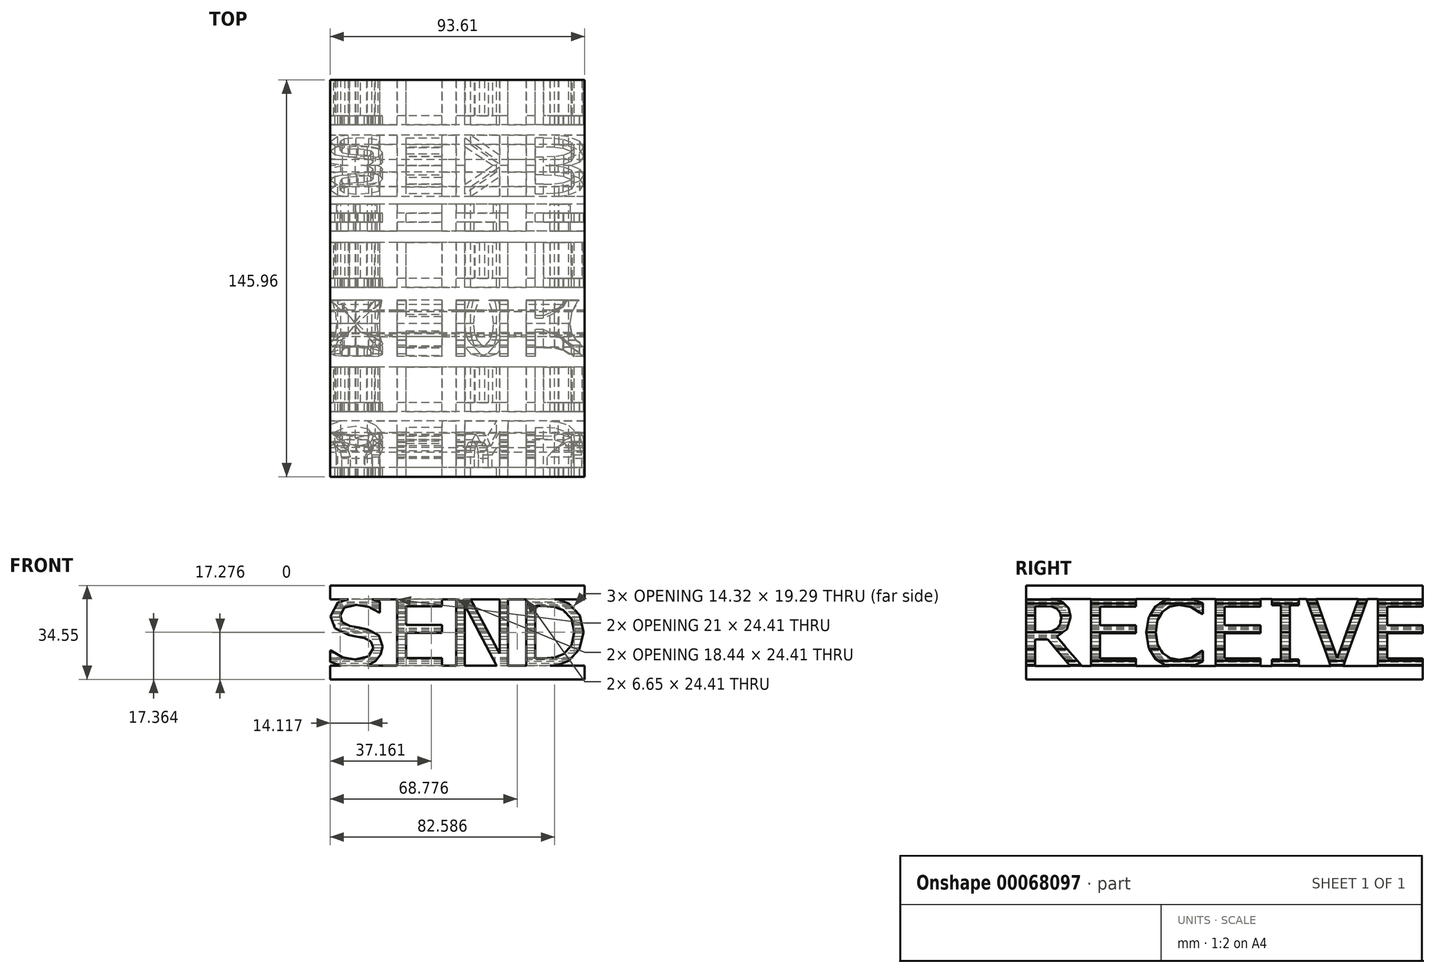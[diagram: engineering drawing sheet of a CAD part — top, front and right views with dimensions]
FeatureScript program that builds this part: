
annotation { "Feature Type Name" : "Feature", "Feature Type Description" : "" }
export const myFeature = defineFeature(function(context is Context, id is Id, definition is map)
    precondition{}
    {
        {
            var Q0;
            Q0=qCreatedBy(makeId("Front.planeOp"),FACE);
            var sketch = newSketch(context, id + "F0", { "sketchPlane" : qUnion([Q0])});
            skLineSegment(sketch, "E0", {"start": v(-25.06, -1.87) * mm, "end": v(-25.75, -4.76) * mm});
            skLineSegment(sketch, "E1", {"start": v(-25.75, -4.76) * mm, "end": v(-27.65, -7.18) * mm});
            skLineSegment(sketch, "E2", {"start": v(-27.65, -7.18) * mm, "end": v(-30.79, -8.85) * mm});
            skLineSegment(sketch, "E3", {"start": v(-35.08, -9.46) * mm, "end": v(-39.95, -8.96) * mm});
            skLineSegment(sketch, "E4", {"start": v(-39.95, -8.96) * mm, "end": v(-44.33, -7.46) * mm});
            skLineSegment(sketch, "E5", {"start": v(-44.33, -7.46) * mm, "end": v(-44.33, -3.3) * mm});
            skLineSegment(sketch, "E6", {"start": v(-769.15, -29.29) * mm, "end": v(-768.92, -29.29) * mm});
            skLineSegment(sketch, "E7", {"start": v(-44.1, -3.3) * mm, "end": v(-39.72, -5.73) * mm});
            skLineSegment(sketch, "E8", {"start": v(-39.72, -5.73) * mm, "end": v(-35.05, -6.59) * mm});
            skLineSegment(sketch, "E9", {"start": v(-35.05, -6.59) * mm, "end": v(-30.25, -5.43) * mm});
            skLineSegment(sketch, "E10", {"start": v(-30.25, -5.43) * mm, "end": v(-28.52, -2.34) * mm});
            skLineSegment(sketch, "E11", {"start": v(-28.52, -2.34) * mm, "end": v(-29.34, 0.11) * mm});
            skLineSegment(sketch, "E12", {"start": v(-29.34, 0.11) * mm, "end": v(-31.8, 1.34) * mm});
            skLineSegment(sketch, "E13", {"start": v(-34.55, 1.9) * mm, "end": v(-37.65, 2.44) * mm});
            skLineSegment(sketch, "E14", {"start": v(-37.65, 2.44) * mm, "end": v(-42.59, 4.85) * mm});
            skLineSegment(sketch, "E15", {"start": v(-42.59, 4.85) * mm, "end": v(-44.18, 9.3) * mm});
            skLineSegment(sketch, "E16", {"start": v(-44.18, 9.3) * mm, "end": v(-41.53, 14.43) * mm});
            skLineSegment(sketch, "E17", {"start": v(-41.53, 14.43) * mm, "end": v(-37.6, 15.61) * mm});
            skLineSegment(sketch, "E18", {"start": v(-34.8, 16.45) * mm, "end": v(-29.96, 15.94) * mm});
            skLineSegment(sketch, "E19", {"start": v(-29.96, 15.94) * mm, "end": v(-26.07, 14.7) * mm});
            skLineSegment(sketch, "E20", {"start": v(-26.07, 14.7) * mm, "end": v(-26.07, 10.77) * mm});
            skLineSegment(sketch, "E21", {"start": v(-675.43, -16.65) * mm, "end": v(-675.67, -16.65) * mm});
            skLineSegment(sketch, "E22", {"start": v(-26.3, 10.77) * mm, "end": v(-30.06, 12.77) * mm});
            skLineSegment(sketch, "E23", {"start": v(-30.06, 12.77) * mm, "end": v(-34.82, 13.58) * mm});
            skLineSegment(sketch, "E24", {"start": v(-34.82, 13.58) * mm, "end": v(-39.11, 12.47) * mm});
            skLineSegment(sketch, "E25", {"start": v(-39.11, 12.47) * mm, "end": v(-40.73, 9.61) * mm});
            skLineSegment(sketch, "E26", {"start": v(-40.73, 9.61) * mm, "end": v(-39.92, 7.16) * mm});
            skLineSegment(sketch, "E27", {"start": v(-39.92, 7.16) * mm, "end": v(-37.08, 5.8) * mm});
            skLineSegment(sketch, "E28", {"start": v(-37.08, 5.8) * mm, "end": v(-34.03, 5.23) * mm});
            skLineSegment(sketch, "E29", {"start": v(-34.03, 5.23) * mm, "end": v(-30.67, 4.54) * mm});
            skLineSegment(sketch, "E30", {"start": v(-30.67, 4.54) * mm, "end": v(-26.47, 2.31) * mm});
            skLineSegment(sketch, "E31", {"start": v(-26.47, 2.31) * mm, "end": v(-25.06, -1.87) * mm});
            skLineSegment(sketch, "E32", {"start": v(-19.72, -9) * mm, "end": v(-19.72, 16) * mm});
            skLineSegment(sketch, "E33", {"start": v(-3.25, 16) * mm, "end": v(-3.25, 13.04) * mm});
            skLineSegment(sketch, "E34", {"start": v(-3.25, 13.04) * mm, "end": v(-16.4, 13.04) * mm});
            skLineSegment(sketch, "E35", {"start": v(-16.4, 13.04) * mm, "end": v(-16.4, 6.19) * mm});
            skLineSegment(sketch, "E36", {"start": v(-16.4, 6.19) * mm, "end": v(-3.25, 6.19) * mm});
            skLineSegment(sketch, "E37", {"start": v(-3.25, 6.19) * mm, "end": v(-3.25, 3.23) * mm});
            skLineSegment(sketch, "E38", {"start": v(-3.25, 3.23) * mm, "end": v(-16.4, 3.23) * mm});
            skLineSegment(sketch, "E39", {"start": v(-16.4, 3.23) * mm, "end": v(-16.4, -6.05) * mm});
            skLineSegment(sketch, "E40", {"start": v(-16.4, -6.05) * mm, "end": v(-3.25, -6.05) * mm});
            skLineSegment(sketch, "E41", {"start": v(-3.25, -6.05) * mm, "end": v(-3.25, -9) * mm});
            skLineSegment(sketch, "E42", {"start": v(17, -9) * mm, "end": v(5.14, 13.36) * mm});
            skLineSegment(sketch, "E43", {"start": v(5.14, 13.36) * mm, "end": v(5.14, -9) * mm});
            skLineSegment(sketch, "E44", {"start": v(2.04, -9) * mm, "end": v(2.04, 16) * mm});
            skLineSegment(sketch, "E45", {"start": v(7.2, 16) * mm, "end": v(18, -4.42) * mm});
            skLineSegment(sketch, "E46", {"start": v(18, -4.42) * mm, "end": v(18, 16) * mm});
            skLineSegment(sketch, "E47", {"start": v(21.11, 16) * mm, "end": v(21.11, -9) * mm});
            skLineSegment(sketch, "E48", {"start": v(48.88, 3.47) * mm, "end": v(47.39, -2.7) * mm});
            skLineSegment(sketch, "E49", {"start": v(47.39, -2.7) * mm, "end": v(43.44, -7) * mm});
            skLineSegment(sketch, "E50", {"start": v(43.44, -7) * mm, "end": v(39.61, -8.54) * mm});
            skLineSegment(sketch, "E51", {"start": v(39.61, -8.54) * mm, "end": v(34.07, -9) * mm});
            skLineSegment(sketch, "E52", {"start": v(27.76, -9) * mm, "end": v(27.76, 16) * mm});
            skLineSegment(sketch, "E53", {"start": v(34, 16) * mm, "end": v(39.82, 15.46) * mm});
            skLineSegment(sketch, "E54", {"start": v(39.82, 15.46) * mm, "end": v(43.48, 14.01) * mm});
            skLineSegment(sketch, "E55", {"start": v(43.48, 14.01) * mm, "end": v(47.45, 9.77) * mm});
            skLineSegment(sketch, "E56", {"start": v(47.45, 9.77) * mm, "end": v(48.88, 3.47) * mm});
            skLineSegment(sketch, "E57", {"start": v(45.4, 3.52) * mm, "end": v(44.38, 8.47) * mm});
            skLineSegment(sketch, "E58", {"start": v(44.38, 8.47) * mm, "end": v(41.33, 11.65) * mm});
            skLineSegment(sketch, "E59", {"start": v(41.33, 11.65) * mm, "end": v(38.19, 12.8) * mm});
            skLineSegment(sketch, "E60", {"start": v(38.19, 12.8) * mm, "end": v(34.2, 13.14) * mm});
            skLineSegment(sketch, "E61", {"start": v(31.08, 13.14) * mm, "end": v(31.08, -6.15) * mm});
            skLineSegment(sketch, "E62", {"start": v(34.2, -6.15) * mm, "end": v(38.39, -5.8) * mm});
            skLineSegment(sketch, "E63", {"start": v(38.39, -5.8) * mm, "end": v(41.68, -4.49) * mm});
            skLineSegment(sketch, "E64", {"start": v(41.68, -4.49) * mm, "end": v(44.47, -1.35) * mm});
            skLineSegment(sketch, "E65", {"start": v(44.47, -1.35) * mm, "end": v(45.4, 3.52) * mm});
            skLineSegment(sketch, "E66", {"start": v(-581.37, -15.69) * mm, "end": v(-581.63, -15.69) * mm});
            skLineSegment(sketch, "E67", {"start": v(-581.6, -29.29) * mm, "end": v(-581.37, -29.29) * mm});
            skLineSegment(sketch, "E68", {"start": v(-34.55, 1.9) * mm, "end": v(-31.8, 1.34) * mm});
            skLineSegment(sketch, "E69", {"start": v(-44.33, -3.3) * mm, "end": v(-44.1, -3.3) * mm});
            skLineSegment(sketch, "E70", {"start": v(-26.3, 10.77) * mm, "end": v(-26.07, 10.77) * mm});
            skLineSegment(sketch, "E71.bottom", {"start": v(-44.34, -13.87) * mm, "end": v(49.27, -13.87) * mm});
            skLineSegment(sketch, "E71.top", {"start": v(-44.34, -8.8) * mm, "end": v(-40.41, -8.8) * mm});
            skLineSegment(sketch, "E71.left", {"start": v(-44.34, -13.87) * mm, "end": v(-44.34, -8.8) * mm});
            skLineSegment(sketch, "E71.right", {"start": v(49.27, -13.87) * mm, "end": v(49.27, -8.8) * mm});
            skLineSegment(sketch, "E72", {"start": v(31.08, 13.14) * mm, "end": v(34.2, 13.14) * mm});
            skLineSegment(sketch, "E73", {"start": v(34.2, -6.15) * mm, "end": v(31.08, -6.15) * mm});
            skLineSegment(sketch, "E74.bottom", {"start": v(-44.34, 15.61) * mm, "end": v(-37.6, 15.61) * mm});
            skLineSegment(sketch, "E74.top", {"start": v(-44.34, 20.68) * mm, "end": v(49.27, 20.68) * mm});
            skLineSegment(sketch, "E74.left", {"start": v(-44.34, 15.61) * mm, "end": v(-44.34, 20.68) * mm});
            skLineSegment(sketch, "E74.right", {"start": v(49.27, 15.61) * mm, "end": v(49.27, 20.68) * mm});
            skLineSegment(sketch, "E75.trimOffspring", {"start": v(-28.92, 15.61) * mm, "end": v(-19.72, 15.61) * mm});
            skLineSegment(sketch, "E76.trimOffspring", {"start": v(-30.68, -8.8) * mm, "end": v(-19.72, -8.8) * mm});
            skLineSegment(sketch, "E77.trimOffspring", {"start": v(-3.25, -8.8) * mm, "end": v(2.04, -8.8) * mm});
            skLineSegment(sketch, "E78.trimOffspring", {"start": v(5.14, -8.8) * mm, "end": v(16.89, -8.8) * mm});
            skLineSegment(sketch, "E79.trimOffspring", {"start": v(-3.25, 15.61) * mm, "end": v(2.04, 15.61) * mm});
            skLineSegment(sketch, "E80.trimOffspring", {"start": v(7.4, 15.61) * mm, "end": v(18, 15.61) * mm});
            skLineSegment(sketch, "E81.trimOffspring", {"start": v(21.11, -8.8) * mm, "end": v(27.76, -8.8) * mm});
            skLineSegment(sketch, "E82.trimOffspring", {"start": v(21.11, 15.61) * mm, "end": v(27.76, 15.61) * mm});
            skLineSegment(sketch, "E83.trimOffspring", {"start": v(38.14, 15.61) * mm, "end": v(49.27, 15.61) * mm});
            skLineSegment(sketch, "E84.trimOffspring", {"start": v(36.5, -8.8) * mm, "end": v(49.27, -8.8) * mm});
            skSolve(sketch);
        }
        {
            var Q0;
            Q0=makeQuery(id+"F0.imprint","IMPRINT",FACE,{"disambiguationData":[TD([[makeQuery(id+"F0.imprint","IMPRINT",EDGE,{"derivedFrom":sQuery(id+"F0.wireOp",EDGE,"E0")}),-1.0]])]});
            extrude(context, id + "F1", {"entities" : qUnion([Q0]), "endBound" : BoundingType.SYMMETRIC, "depth" : 205 * mm});
        }
        {
            var Q0;
            Q0=qCreatedBy(makeId("Right.planeOp"),FACE);
            var sketch = newSketch(context, id + "F2", { "sketchPlane" : qUnion([Q0])});
            skLineSegment(sketch, "E85", {"start": v(-134.38, -6.8) * mm, "end": v(-134.14, -6.8) * mm});
            skLineSegment(sketch, "E86", {"start": v(-116.1, 7.28) * mm, "end": v(-116.34, 7.28) * mm});
            skLineSegment(sketch, "E87", {"start": v(-43.67, -9.1) * mm, "end": v(-52.03, 0.84) * mm});
            skLineSegment(sketch, "E88", {"start": v(-52.03, 0.84) * mm, "end": v(-56.71, 0.84) * mm});
            skLineSegment(sketch, "E89", {"start": v(-56.71, 0.84) * mm, "end": v(-56.71, -9.1) * mm});
            skLineSegment(sketch, "E90", {"start": v(-60.04, -8.72) * mm, "end": v(-60.04, 16.28) * mm});
            skLineSegment(sketch, "E91", {"start": v(-53.04, 15.9) * mm, "end": v(-49.26, 15.6) * mm});
            skLineSegment(sketch, "E92", {"start": v(-49.26, 15.6) * mm, "end": v(-46.54, 14.55) * mm});
            skLineSegment(sketch, "E93", {"start": v(-46.54, 14.55) * mm, "end": v(-44.42, 12.39) * mm});
            skLineSegment(sketch, "E94", {"start": v(-44.42, 12.39) * mm, "end": v(-43.65, 9.1) * mm});
            skLineSegment(sketch, "E95", {"start": v(-43.65, 9.1) * mm, "end": v(-45, 4.56) * mm});
            skLineSegment(sketch, "E96", {"start": v(-45, 4.56) * mm, "end": v(-48.75, 1.83) * mm});
            skLineSegment(sketch, "E97", {"start": v(-48.75, 1.83) * mm, "end": v(-39.35, -9.1) * mm});
            skLineSegment(sketch, "E98", {"start": v(-47.13, 8.86) * mm, "end": v(-47.51, 10.76) * mm});
            skLineSegment(sketch, "E99", {"start": v(-47.51, 10.76) * mm, "end": v(-48.75, 12.17) * mm});
            skLineSegment(sketch, "E100", {"start": v(-48.75, 12.17) * mm, "end": v(-50.47, 12.84) * mm});
            skLineSegment(sketch, "E101", {"start": v(-50.47, 12.84) * mm, "end": v(-52.8, 13.04) * mm});
            skLineSegment(sketch, "E102", {"start": v(-52.8, 13.04) * mm, "end": v(-56.71, 13.04) * mm});
            skLineSegment(sketch, "E103", {"start": v(-56.71, 13.04) * mm, "end": v(-56.71, 3.6) * mm});
            skLineSegment(sketch, "E104", {"start": v(-56.71, 3.6) * mm, "end": v(-53.35, 3.6) * mm});
            skLineSegment(sketch, "E105", {"start": v(-53.35, 3.6) * mm, "end": v(-50.6, 3.87) * mm});
            skLineSegment(sketch, "E106", {"start": v(-50.6, 3.87) * mm, "end": v(-48.6, 4.92) * mm});
            skLineSegment(sketch, "E107", {"start": v(-48.6, 4.92) * mm, "end": v(-47.5, 6.53) * mm});
            skLineSegment(sketch, "E108", {"start": v(-47.5, 6.53) * mm, "end": v(-47.13, 8.86) * mm});
            skLineSegment(sketch, "E109", {"start": v(-36.13, -9.1) * mm, "end": v(-36.13, 15.9) * mm});
            skLineSegment(sketch, "E110", {"start": v(-19.66, 15.9) * mm, "end": v(-19.66, 12.94) * mm});
            skLineSegment(sketch, "E111", {"start": v(-19.66, 12.94) * mm, "end": v(-32.8, 12.94) * mm});
            skLineSegment(sketch, "E112", {"start": v(-32.8, 12.94) * mm, "end": v(-32.8, 6.1) * mm});
            skLineSegment(sketch, "E113", {"start": v(-32.8, 6.1) * mm, "end": v(-19.66, 6.1) * mm});
            skLineSegment(sketch, "E114", {"start": v(-19.66, 6.1) * mm, "end": v(-19.66, 3.14) * mm});
            skLineSegment(sketch, "E115", {"start": v(-19.66, 3.14) * mm, "end": v(-32.8, 3.14) * mm});
            skLineSegment(sketch, "E116", {"start": v(-32.8, 3.14) * mm, "end": v(-32.8, -6.15) * mm});
            skLineSegment(sketch, "E117", {"start": v(-32.8, -6.15) * mm, "end": v(-19.66, -6.15) * mm});
            skLineSegment(sketch, "E118", {"start": v(-19.66, -6.15) * mm, "end": v(-19.66, -9.1) * mm});
            skLineSegment(sketch, "E119", {"start": v(4.94, -7.3) * mm, "end": v(3.26, -8.05) * mm});
            skLineSegment(sketch, "E120", {"start": v(3.26, -8.05) * mm, "end": v(1.31, -8.78) * mm});
            skLineSegment(sketch, "E121", {"start": v(1.31, -8.78) * mm, "end": v(-0.92, -9.32) * mm});
            skLineSegment(sketch, "E122", {"start": v(-3.56, -9.56) * mm, "end": v(-8.5, -8.8) * mm});
            skLineSegment(sketch, "E123", {"start": v(-8.5, -8.8) * mm, "end": v(-12.37, -6.4) * mm});
            skLineSegment(sketch, "E124", {"start": v(-12.37, -6.4) * mm, "end": v(-14.89, -2.35) * mm});
            skLineSegment(sketch, "E125", {"start": v(-14.89, -2.35) * mm, "end": v(-15.8, 3.37) * mm});
            skLineSegment(sketch, "E126", {"start": v(-15.8, 3.37) * mm, "end": v(-14.92, 8.9) * mm});
            skLineSegment(sketch, "E127", {"start": v(-14.92, 8.9) * mm, "end": v(-12.4, 13) * mm});
            skLineSegment(sketch, "E128", {"start": v(-12.4, 13) * mm, "end": v(-8.56, 15.5) * mm});
            skLineSegment(sketch, "E129", {"start": v(-8.56, 15.5) * mm, "end": v(-3.54, 16.35) * mm});
            skLineSegment(sketch, "E130", {"start": v(0.47, 15.86) * mm, "end": v(4.94, 14.15) * mm});
            skLineSegment(sketch, "E131", {"start": v(4.94, 14.15) * mm, "end": v(4.94, 10.2) * mm});
            skLineSegment(sketch, "E132", {"start": v(53.4, 6.8) * mm, "end": v(53.15, 6.8) * mm});
            skLineSegment(sketch, "E133", {"start": v(4.69, 10.2) * mm, "end": v(0.6, 12.72) * mm});
            skLineSegment(sketch, "E134", {"start": v(0.6, 12.72) * mm, "end": v(-3.76, 13.51) * mm});
            skLineSegment(sketch, "E135", {"start": v(-3.76, 13.51) * mm, "end": v(-7.18, 12.9) * mm});
            skLineSegment(sketch, "E136", {"start": v(-7.18, 12.9) * mm, "end": v(-9.89, 11) * mm});
            skLineSegment(sketch, "E137", {"start": v(-9.89, 11) * mm, "end": v(-11.7, 7.8) * mm});
            skLineSegment(sketch, "E138", {"start": v(-11.7, 7.8) * mm, "end": v(-12.34, 3.37) * mm});
            skLineSegment(sketch, "E139", {"start": v(-12.34, 3.37) * mm, "end": v(-11.63, -1.16) * mm});
            skLineSegment(sketch, "E140", {"start": v(-11.63, -1.16) * mm, "end": v(-9.78, -4.25) * mm});
            skLineSegment(sketch, "E141", {"start": v(-9.78, -4.25) * mm, "end": v(-7.05, -6.1) * mm});
            skLineSegment(sketch, "E142", {"start": v(-7.05, -6.1) * mm, "end": v(-3.72, -6.69) * mm});
            skLineSegment(sketch, "E143", {"start": v(-3.72, -6.69) * mm, "end": v(0.78, -5.86) * mm});
            skLineSegment(sketch, "E144", {"start": v(0.78, -5.86) * mm, "end": v(4.7, -3.4) * mm});
            skLineSegment(sketch, "E145", {"start": v(53.16, -6.8) * mm, "end": v(53.4, -6.8) * mm});
            skLineSegment(sketch, "E146", {"start": v(4.94, -3.4) * mm, "end": v(4.94, -7.3) * mm});
            skLineSegment(sketch, "E147", {"start": v(9.67, -9.1) * mm, "end": v(9.67, 15.9) * mm});
            skLineSegment(sketch, "E148", {"start": v(26.15, 15.9) * mm, "end": v(26.15, 12.94) * mm});
            skLineSegment(sketch, "E149", {"start": v(26.15, 12.94) * mm, "end": v(13, 12.94) * mm});
            skLineSegment(sketch, "E150", {"start": v(13, 12.94) * mm, "end": v(13, 6.1) * mm});
            skLineSegment(sketch, "E151", {"start": v(13, 6.1) * mm, "end": v(26.15, 6.1) * mm});
            skLineSegment(sketch, "E152", {"start": v(26.15, 6.1) * mm, "end": v(26.15, 3.14) * mm});
            skLineSegment(sketch, "E153", {"start": v(26.15, 3.14) * mm, "end": v(13, 3.14) * mm});
            skLineSegment(sketch, "E154", {"start": v(13, 3.14) * mm, "end": v(13, -6.15) * mm});
            skLineSegment(sketch, "E155", {"start": v(13, -6.15) * mm, "end": v(26.15, -6.15) * mm});
            skLineSegment(sketch, "E156", {"start": v(26.15, -6.15) * mm, "end": v(26.15, -9.1) * mm});
            skLineSegment(sketch, "E157", {"start": v(30.38, -9.1) * mm, "end": v(30.38, -6.55) * mm});
            skLineSegment(sketch, "E158", {"start": v(30.38, -6.55) * mm, "end": v(33.65, -6.55) * mm});
            skLineSegment(sketch, "E159", {"start": v(33.65, -6.55) * mm, "end": v(33.65, 13.34) * mm});
            skLineSegment(sketch, "E160", {"start": v(33.65, 13.34) * mm, "end": v(30.38, 13.34) * mm});
            skLineSegment(sketch, "E161", {"start": v(30.38, 13.34) * mm, "end": v(30.38, 15.9) * mm});
            skLineSegment(sketch, "E162", {"start": v(40.25, 15.9) * mm, "end": v(40.25, 13.34) * mm});
            skLineSegment(sketch, "E163", {"start": v(40.25, 13.34) * mm, "end": v(36.97, 13.34) * mm});
            skLineSegment(sketch, "E164", {"start": v(36.97, 13.34) * mm, "end": v(36.97, -6.55) * mm});
            skLineSegment(sketch, "E165", {"start": v(36.97, -6.55) * mm, "end": v(40.25, -6.55) * mm});
            skLineSegment(sketch, "E166", {"start": v(40.25, -6.55) * mm, "end": v(40.25, -9.1) * mm});
            skLineSegment(sketch, "E167", {"start": v(65.65, 15.9) * mm, "end": v(56.55, -9.1) * mm});
            skLineSegment(sketch, "E168", {"start": v(52.12, -9.1) * mm, "end": v(43.02, 15.9) * mm});
            skLineSegment(sketch, "E169", {"start": v(46.58, 15.9) * mm, "end": v(54.42, -6.1) * mm});
            skLineSegment(sketch, "E170", {"start": v(54.42, -6.1) * mm, "end": v(62.26, 15.9) * mm});
            skLineSegment(sketch, "E171", {"start": v(69.45, -9.1) * mm, "end": v(69.45, 15.9) * mm});
            skLineSegment(sketch, "E172", {"start": v(85.92, 15.9) * mm, "end": v(85.92, 12.94) * mm});
            skLineSegment(sketch, "E173", {"start": v(85.92, 12.94) * mm, "end": v(72.77, 12.94) * mm});
            skLineSegment(sketch, "E174", {"start": v(72.77, 12.94) * mm, "end": v(72.77, 6.1) * mm});
            skLineSegment(sketch, "E175", {"start": v(72.77, 6.1) * mm, "end": v(85.92, 6.1) * mm});
            skLineSegment(sketch, "E176", {"start": v(85.92, 6.1) * mm, "end": v(85.92, 3.14) * mm});
            skLineSegment(sketch, "E177", {"start": v(85.92, 3.14) * mm, "end": v(72.77, 3.14) * mm});
            skLineSegment(sketch, "E178", {"start": v(72.77, 3.14) * mm, "end": v(72.77, -6.15) * mm});
            skLineSegment(sketch, "E179", {"start": v(72.77, -6.15) * mm, "end": v(85.92, -6.15) * mm});
            skLineSegment(sketch, "E180", {"start": v(85.92, -6.15) * mm, "end": v(85.92, -9.1) * mm});
            skLineSegment(sketch, "E181.bottom", {"start": v(-51, 15.73) * mm, "end": v(-36.13, 15.73) * mm});
            skLineSegment(sketch, "E181.top", {"start": v(-60.04, 20.73) * mm, "end": v(85.92, 20.73) * mm});
            skLineSegment(sketch, "E181.left", {"start": v(-60.04, 15.73) * mm, "end": v(-60.04, 20.73) * mm});
            skLineSegment(sketch, "E181.right", {"start": v(85.92, 15.73) * mm, "end": v(85.92, 20.73) * mm});
            skLineSegment(sketch, "E182.bottom", {"start": v(-56.71, -8.96) * mm, "end": v(-43.78, -8.96) * mm});
            skLineSegment(sketch, "E182.top", {"start": v(-60.04, -13.96) * mm, "end": v(85.92, -13.96) * mm});
            skLineSegment(sketch, "E182.left", {"start": v(-60.04, -8.96) * mm, "end": v(-60.04, -13.96) * mm});
            skLineSegment(sketch, "E182.right", {"start": v(85.92, -8.96) * mm, "end": v(85.92, -13.96) * mm});
            skLineSegment(sketch, "E183", {"start": v(-60.04, -9.1) * mm, "end": v(-60.04, -8.72) * mm});
            skLineSegment(sketch, "E184.trimOffspring", {"start": v(-39.47, -8.96) * mm, "end": v(-36.13, -8.96) * mm});
            skLineSegment(sketch, "E185.trimOffspring", {"start": v(-19.66, -8.96) * mm, "end": v(-7.45, -8.96) * mm});
            skPoint(sketch, "E186.start.orphan", {"position": v(-60.04, 15.9) * mm});
            skLineSegment(sketch, "E187.trimOffspring", {"start": v(-19.66, 15.73) * mm, "end": v(-7.15, 15.73) * mm});
            skLineSegment(sketch, "E188.trimOffspring", {"start": v(0.8, 15.73) * mm, "end": v(9.67, 15.73) * mm});
            skLineSegment(sketch, "E189.trimOffspring", {"start": v(0.57, -8.96) * mm, "end": v(9.67, -8.96) * mm});
            skLineSegment(sketch, "E190.trimOffspring", {"start": v(26.15, 15.73) * mm, "end": v(30.38, 15.73) * mm});
            skLineSegment(sketch, "E191.trimOffspring", {"start": v(40.25, 15.73) * mm, "end": v(43.08, 15.73) * mm});
            skLineSegment(sketch, "E192.trimOffspring", {"start": v(46.64, 15.73) * mm, "end": v(62.2, 15.73) * mm});
            skLineSegment(sketch, "E193.trimOffspring", {"start": v(26.15, -8.96) * mm, "end": v(30.38, -8.96) * mm});
            skLineSegment(sketch, "E194.trimOffspring", {"start": v(40.25, -8.96) * mm, "end": v(52.07, -8.96) * mm});
            skLineSegment(sketch, "E195.trimOffspring", {"start": v(56.6, -8.96) * mm, "end": v(69.45, -8.96) * mm});
            skLineSegment(sketch, "E196.trimOffspring", {"start": v(65.6, 15.73) * mm, "end": v(69.45, 15.73) * mm});
            skPoint(sketch, "E197.end.orphan", {"position": v(85.92, 16.28) * mm});
            skPoint(sketch, "E198.start.orphan", {"position": v(85.92, -9.1) * mm});
            skLineSegment(sketch, "E199", {"start": v(4.7, -3.4) * mm, "end": v(4.94, -3.4) * mm});
            skLineSegment(sketch, "E200", {"start": v(4.69, 10.2) * mm, "end": v(4.94, 10.2) * mm});
            skSolve(sketch);
        }
        {
            var Q0;
            {var subQ38=sQuery(id+"F2.wireOp",EDGE,"E88");Q0=makeQuery(id+"F2.imprint","IMPRINT",FACE,{"disambiguationData":[TD([[makeQuery(id+"F2.imprint","IMPRINT",EDGE,{"derivedFrom":subQ38}),-1.0]])]});}
            extrude(context, id + "F3", {"entities" : qUnion([Q0]), "endBound" : BoundingType.SYMMETRIC, "depth" : 222 * mm});
        }
        {
            var Q0;
            Q0=makeQuery(id+"F1.opExtrude","SWEPT_BODY",BODY,{"disambiguationData":[OSD([sQuery(id+"F0.wireOp",EDGE,"E0"),sQuery(id+"F0.wireOp",EDGE,"E1"),sQuery(id+"F0.wireOp",EDGE,"E2"),sQuery(id+"F0.wireOp",EDGE,"E4"),sQuery(id+"F0.wireOp",EDGE,"E5"),sQuery(id+"F0.wireOp",EDGE,"E7"),sQuery(id+"F0.wireOp",EDGE,"E8"),sQuery(id+"F0.wireOp",EDGE,"E9"),sQuery(id+"F0.wireOp",EDGE,"E10"),sQuery(id+"F0.wireOp",EDGE,"E11"),sQuery(id+"F0.wireOp",EDGE,"E12"),sQuery(id+"F0.wireOp",EDGE,"E13"),sQuery(id+"F0.wireOp",EDGE,"E14"),sQuery(id+"F0.wireOp",EDGE,"E15"),sQuery(id+"F0.wireOp",EDGE,"E16"),sQuery(id+"F0.wireOp",EDGE,"E17"),sQuery(id+"F0.wireOp",EDGE,"E19"),sQuery(id+"F0.wireOp",EDGE,"E20"),sQuery(id+"F0.wireOp",EDGE,"E22"),sQuery(id+"F0.wireOp",EDGE,"E23"),sQuery(id+"F0.wireOp",EDGE,"E24"),sQuery(id+"F0.wireOp",EDGE,"E25"),sQuery(id+"F0.wireOp",EDGE,"E26"),sQuery(id+"F0.wireOp",EDGE,"E27"),sQuery(id+"F0.wireOp",EDGE,"E28"),sQuery(id+"F0.wireOp",EDGE,"E29"),sQuery(id+"F0.wireOp",EDGE,"E30"),sQuery(id+"F0.wireOp",EDGE,"E31"),sQuery(id+"F0.wireOp",EDGE,"E32"),sQuery(id+"F0.wireOp",EDGE,"E33"),sQuery(id+"F0.wireOp",EDGE,"E34"),sQuery(id+"F0.wireOp",EDGE,"E35"),sQuery(id+"F0.wireOp",EDGE,"E36"),sQuery(id+"F0.wireOp",EDGE,"E37"),sQuery(id+"F0.wireOp",EDGE,"E38"),sQuery(id+"F0.wireOp",EDGE,"E39"),sQuery(id+"F0.wireOp",EDGE,"E40"),sQuery(id+"F0.wireOp",EDGE,"E41"),sQuery(id+"F0.wireOp",EDGE,"E42"),sQuery(id+"F0.wireOp",EDGE,"E43"),sQuery(id+"F0.wireOp",EDGE,"E44"),sQuery(id+"F0.wireOp",EDGE,"E45"),sQuery(id+"F0.wireOp",EDGE,"E46"),sQuery(id+"F0.wireOp",EDGE,"E47"),sQuery(id+"F0.wireOp",EDGE,"E48"),sQuery(id+"F0.wireOp",EDGE,"E49"),sQuery(id+"F0.wireOp",EDGE,"E50"),sQuery(id+"F0.wireOp",EDGE,"E51"),sQuery(id+"F0.wireOp",EDGE,"E52"),sQuery(id+"F0.wireOp",EDGE,"E53"),sQuery(id+"F0.wireOp",EDGE,"E54"),sQuery(id+"F0.wireOp",EDGE,"E55"),sQuery(id+"F0.wireOp",EDGE,"E56"),sQuery(id+"F0.wireOp",EDGE,"E57"),sQuery(id+"F0.wireOp",EDGE,"E58"),sQuery(id+"F0.wireOp",EDGE,"E59"),sQuery(id+"F0.wireOp",EDGE,"E60"),sQuery(id+"F0.wireOp",EDGE,"E61"),sQuery(id+"F0.wireOp",EDGE,"E62"),sQuery(id+"F0.wireOp",EDGE,"E63"),sQuery(id+"F0.wireOp",EDGE,"E64"),sQuery(id+"F0.wireOp",EDGE,"E65"),sQuery(id+"F0.wireOp",EDGE,"E68"),sQuery(id+"F0.wireOp",EDGE,"E69"),sQuery(id+"F0.wireOp",EDGE,"E70"),sQuery(id+"F0.wireOp",EDGE,"E71.bottom"),sQuery(id+"F0.wireOp",EDGE,"E71.top"),sQuery(id+"F0.wireOp",EDGE,"E71.left"),sQuery(id+"F0.wireOp",EDGE,"E71.right"),sQuery(id+"F0.wireOp",EDGE,"E72"),sQuery(id+"F0.wireOp",EDGE,"E73"),sQuery(id+"F0.wireOp",EDGE,"E74.bottom"),sQuery(id+"F0.wireOp",EDGE,"E74.top"),sQuery(id+"F0.wireOp",EDGE,"E74.left"),sQuery(id+"F0.wireOp",EDGE,"E74.right"),sQuery(id+"F0.wireOp",EDGE,"E75.trimOffspring"),sQuery(id+"F0.wireOp",EDGE,"E76.trimOffspring"),sQuery(id+"F0.wireOp",EDGE,"E77.trimOffspring"),sQuery(id+"F0.wireOp",EDGE,"E78.trimOffspring"),sQuery(id+"F0.wireOp",EDGE,"E79.trimOffspring"),sQuery(id+"F0.wireOp",EDGE,"E80.trimOffspring"),sQuery(id+"F0.wireOp",EDGE,"E81.trimOffspring"),sQuery(id+"F0.wireOp",EDGE,"E82.trimOffspring"),sQuery(id+"F0.wireOp",EDGE,"E83.trimOffspring"),sQuery(id+"F0.wireOp",EDGE,"E84.trimOffspring")])]});
            var Q1;
            Q1=makeQuery(id+"F3.opExtrude","SWEPT_BODY",BODY,{"disambiguationData":[OSD([sQuery(id+"F2.wireOp",EDGE,"E87"),sQuery(id+"F2.wireOp",EDGE,"E88"),sQuery(id+"F2.wireOp",EDGE,"E89"),sQuery(id+"F2.wireOp",EDGE,"E90"),sQuery(id+"F2.wireOp",EDGE,"E91"),sQuery(id+"F2.wireOp",EDGE,"E92"),sQuery(id+"F2.wireOp",EDGE,"E93"),sQuery(id+"F2.wireOp",EDGE,"E94"),sQuery(id+"F2.wireOp",EDGE,"E95"),sQuery(id+"F2.wireOp",EDGE,"E96"),sQuery(id+"F2.wireOp",EDGE,"E97"),sQuery(id+"F2.wireOp",EDGE,"E98"),sQuery(id+"F2.wireOp",EDGE,"E99"),sQuery(id+"F2.wireOp",EDGE,"E100"),sQuery(id+"F2.wireOp",EDGE,"E101"),sQuery(id+"F2.wireOp",EDGE,"E102"),sQuery(id+"F2.wireOp",EDGE,"E103"),sQuery(id+"F2.wireOp",EDGE,"E104"),sQuery(id+"F2.wireOp",EDGE,"E105"),sQuery(id+"F2.wireOp",EDGE,"E106"),sQuery(id+"F2.wireOp",EDGE,"E107"),sQuery(id+"F2.wireOp",EDGE,"E108"),sQuery(id+"F2.wireOp",EDGE,"E109"),sQuery(id+"F2.wireOp",EDGE,"E110"),sQuery(id+"F2.wireOp",EDGE,"E111"),sQuery(id+"F2.wireOp",EDGE,"E112"),sQuery(id+"F2.wireOp",EDGE,"E113"),sQuery(id+"F2.wireOp",EDGE,"E114"),sQuery(id+"F2.wireOp",EDGE,"E115"),sQuery(id+"F2.wireOp",EDGE,"E116"),sQuery(id+"F2.wireOp",EDGE,"E117"),sQuery(id+"F2.wireOp",EDGE,"E118"),sQuery(id+"F2.wireOp",EDGE,"E119"),sQuery(id+"F2.wireOp",EDGE,"E120"),sQuery(id+"F2.wireOp",EDGE,"E121"),sQuery(id+"F2.wireOp",EDGE,"E122"),sQuery(id+"F2.wireOp",EDGE,"E123"),sQuery(id+"F2.wireOp",EDGE,"E124"),sQuery(id+"F2.wireOp",EDGE,"E125"),sQuery(id+"F2.wireOp",EDGE,"E126"),sQuery(id+"F2.wireOp",EDGE,"E127"),sQuery(id+"F2.wireOp",EDGE,"E128"),sQuery(id+"F2.wireOp",EDGE,"E129"),sQuery(id+"F2.wireOp",EDGE,"E130"),sQuery(id+"F2.wireOp",EDGE,"E131"),sQuery(id+"F2.wireOp",EDGE,"E133"),sQuery(id+"F2.wireOp",EDGE,"E134"),sQuery(id+"F2.wireOp",EDGE,"E135"),sQuery(id+"F2.wireOp",EDGE,"E136"),sQuery(id+"F2.wireOp",EDGE,"E137"),sQuery(id+"F2.wireOp",EDGE,"E138"),sQuery(id+"F2.wireOp",EDGE,"E139"),sQuery(id+"F2.wireOp",EDGE,"E140"),sQuery(id+"F2.wireOp",EDGE,"E141"),sQuery(id+"F2.wireOp",EDGE,"E142"),sQuery(id+"F2.wireOp",EDGE,"E143"),sQuery(id+"F2.wireOp",EDGE,"E144"),sQuery(id+"F2.wireOp",EDGE,"E146"),sQuery(id+"F2.wireOp",EDGE,"E147"),sQuery(id+"F2.wireOp",EDGE,"E148"),sQuery(id+"F2.wireOp",EDGE,"E149"),sQuery(id+"F2.wireOp",EDGE,"E150"),sQuery(id+"F2.wireOp",EDGE,"E151"),sQuery(id+"F2.wireOp",EDGE,"E152"),sQuery(id+"F2.wireOp",EDGE,"E153"),sQuery(id+"F2.wireOp",EDGE,"E154"),sQuery(id+"F2.wireOp",EDGE,"E155"),sQuery(id+"F2.wireOp",EDGE,"E156"),sQuery(id+"F2.wireOp",EDGE,"E157"),sQuery(id+"F2.wireOp",EDGE,"E158"),sQuery(id+"F2.wireOp",EDGE,"E159"),sQuery(id+"F2.wireOp",EDGE,"E160"),sQuery(id+"F2.wireOp",EDGE,"E161"),sQuery(id+"F2.wireOp",EDGE,"E162"),sQuery(id+"F2.wireOp",EDGE,"E163"),sQuery(id+"F2.wireOp",EDGE,"E164"),sQuery(id+"F2.wireOp",EDGE,"E165"),sQuery(id+"F2.wireOp",EDGE,"E166"),sQuery(id+"F2.wireOp",EDGE,"E167"),sQuery(id+"F2.wireOp",EDGE,"E168"),sQuery(id+"F2.wireOp",EDGE,"E169"),sQuery(id+"F2.wireOp",EDGE,"E170"),sQuery(id+"F2.wireOp",EDGE,"E171"),sQuery(id+"F2.wireOp",EDGE,"E172"),sQuery(id+"F2.wireOp",EDGE,"E173"),sQuery(id+"F2.wireOp",EDGE,"E174"),sQuery(id+"F2.wireOp",EDGE,"E175"),sQuery(id+"F2.wireOp",EDGE,"E176"),sQuery(id+"F2.wireOp",EDGE,"E177"),sQuery(id+"F2.wireOp",EDGE,"E178"),sQuery(id+"F2.wireOp",EDGE,"E179"),sQuery(id+"F2.wireOp",EDGE,"E180"),sQuery(id+"F2.wireOp",EDGE,"E181.bottom"),sQuery(id+"F2.wireOp",EDGE,"E181.top"),sQuery(id+"F2.wireOp",EDGE,"E181.left"),sQuery(id+"F2.wireOp",EDGE,"E181.right"),sQuery(id+"F2.wireOp",EDGE,"E182.bottom"),sQuery(id+"F2.wireOp",EDGE,"E182.top"),sQuery(id+"F2.wireOp",EDGE,"E182.left"),sQuery(id+"F2.wireOp",EDGE,"E182.right"),sQuery(id+"F2.wireOp",EDGE,"E183"),sQuery(id+"F2.wireOp",EDGE,"E184.trimOffspring"),sQuery(id+"F2.wireOp",EDGE,"E185.trimOffspring"),sQuery(id+"F2.wireOp",EDGE,"E187.trimOffspring"),sQuery(id+"F2.wireOp",EDGE,"E188.trimOffspring"),sQuery(id+"F2.wireOp",EDGE,"E189.trimOffspring"),sQuery(id+"F2.wireOp",EDGE,"E190.trimOffspring"),sQuery(id+"F2.wireOp",EDGE,"E191.trimOffspring"),sQuery(id+"F2.wireOp",EDGE,"E192.trimOffspring"),sQuery(id+"F2.wireOp",EDGE,"E193.trimOffspring"),sQuery(id+"F2.wireOp",EDGE,"E194.trimOffspring"),sQuery(id+"F2.wireOp",EDGE,"E195.trimOffspring"),sQuery(id+"F2.wireOp",EDGE,"E196.trimOffspring"),sQuery(id+"F2.wireOp",EDGE,"E199"),sQuery(id+"F2.wireOp",EDGE,"E200")])]});
            booleanBodies(context, id + "F4", {"operationType" : BooleanOperationType.INTERSECTION, "tools" : qUnion([Q0, Q1])});
        }
    });
